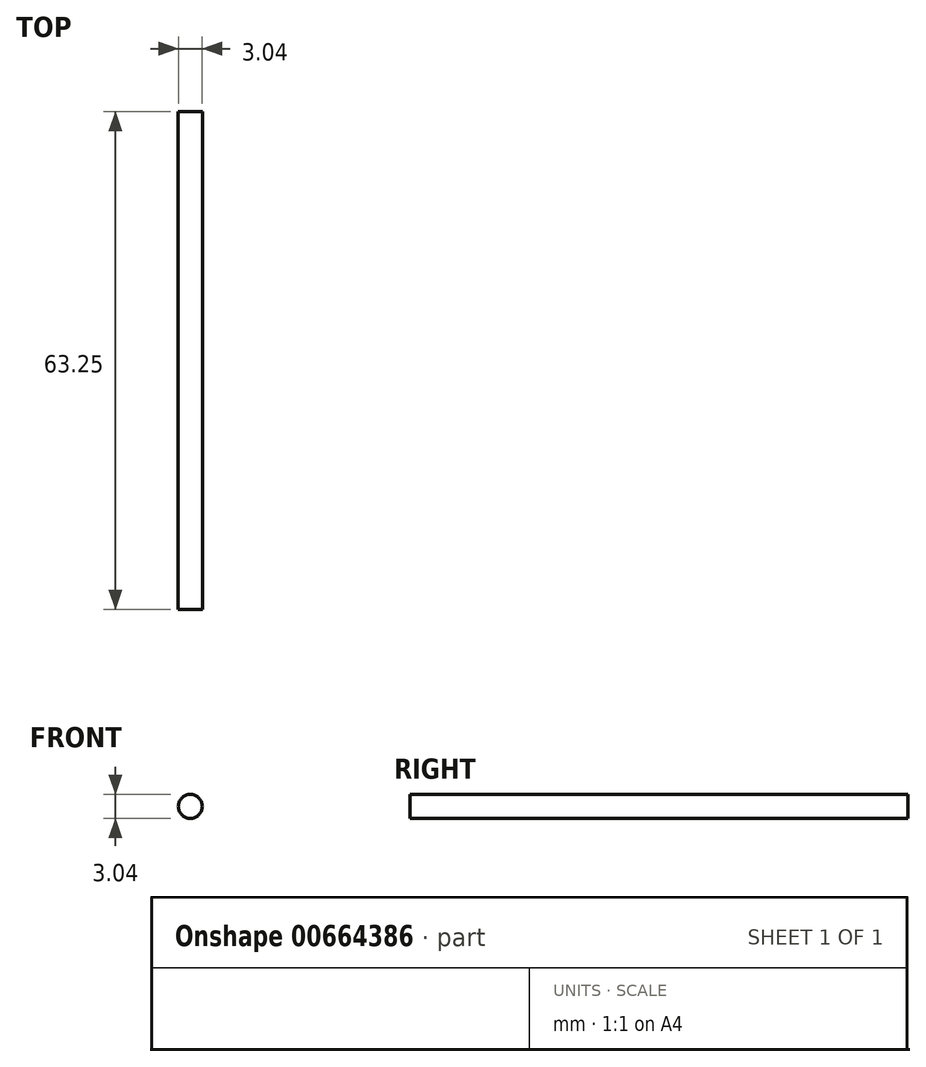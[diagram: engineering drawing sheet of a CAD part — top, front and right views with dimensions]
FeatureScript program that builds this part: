
annotation { "Feature Type Name" : "Feature", "Feature Type Description" : "" }
export const myFeature = defineFeature(function(context is Context, id is Id, definition is map)
    precondition{}
    {
        {
            var Q0;
            Q0=qCreatedBy(makeId("Front.planeOp"),FACE);
            var sketch = newSketch(context, id + "F0", { "sketchPlane" : qUnion([Q0])});
            skCircle(sketch, "E0", {"center": v(0, 0) * mm, "radius": 1.52 * mm});
            skSolve(sketch);
        }
        {
            var Q0;
            Q0 = qSketchRegion(id + "F0", true);
            extrude(context, id + "F1", {"entities" : qUnion([Q0]), "depth" : 63.25 * mm, "offsetDistance" : 25.4 * mm});
        }
    });
